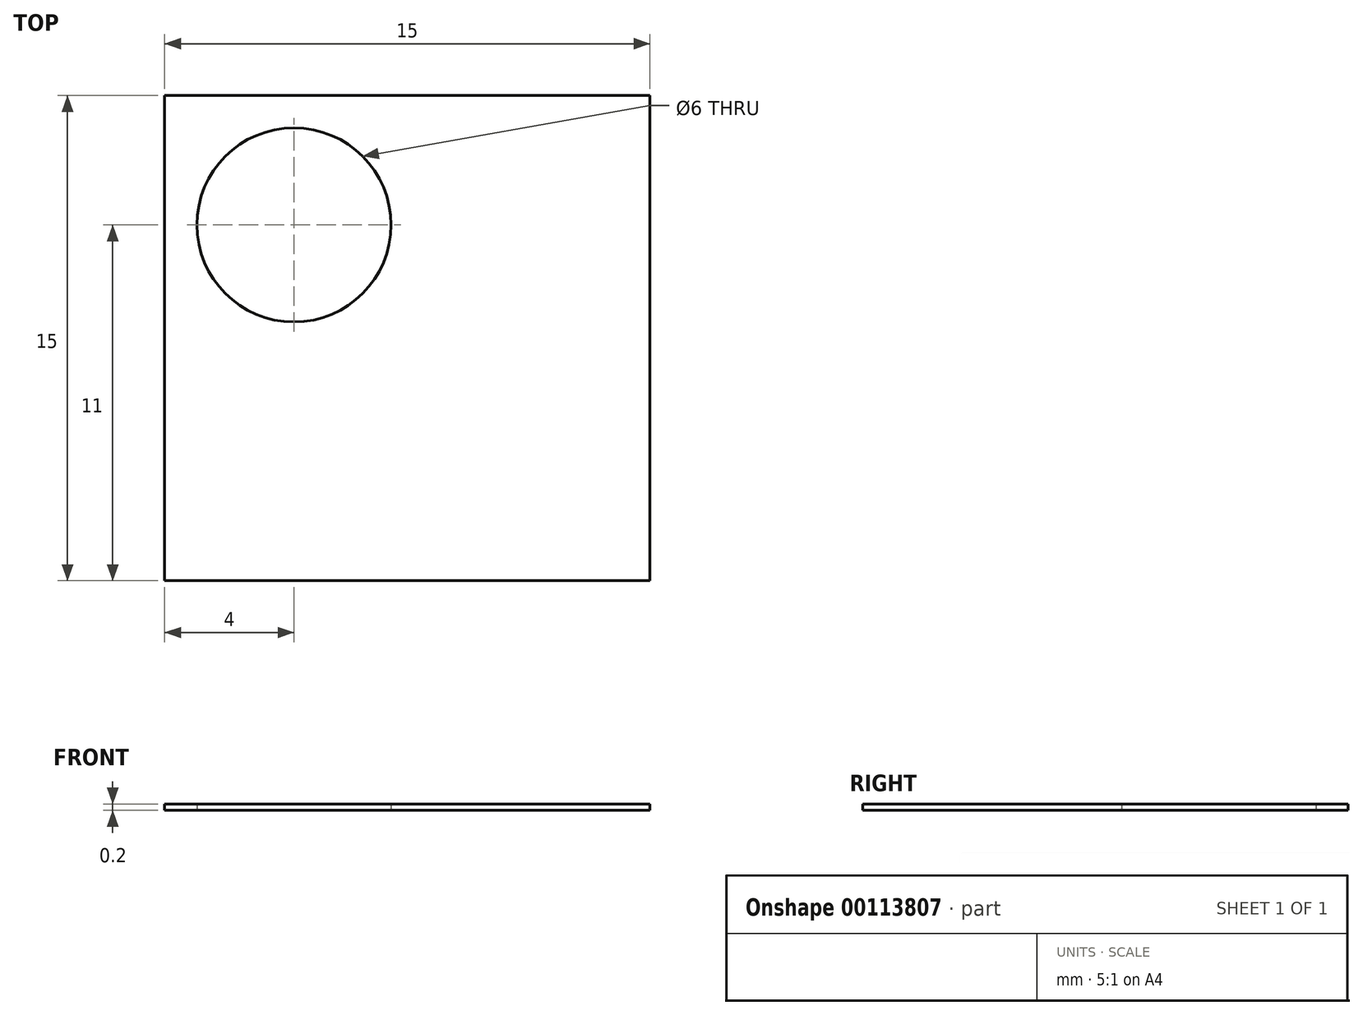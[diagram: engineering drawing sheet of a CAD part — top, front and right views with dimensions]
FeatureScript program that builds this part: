
annotation { "Feature Type Name" : "Feature", "Feature Type Description" : "" }
export const myFeature = defineFeature(function(context is Context, id is Id, definition is map)
    precondition{}
    {
        {
            var Q0;
            Q0=qCreatedBy(makeId("Top.planeOp"),FACE);
            var sketch = newSketch(context, id + "F0", { "sketchPlane" : qUnion([Q0])});
            skLineSegment(sketch, "E0.bottom", {"start": v(0, 15) * mm, "end": v(15, 15) * mm});
            skLineSegment(sketch, "E0.top", {"start": v(0, 0) * mm, "end": v(15, 0) * mm});
            skLineSegment(sketch, "E0.left", {"start": v(0, 15) * mm, "end": v(0, 0) * mm});
            skLineSegment(sketch, "E0.right", {"start": v(15, 15) * mm, "end": v(15, 0) * mm});
            skCircle(sketch, "E1", {"center": v(4, 11) * mm, "radius": 3 * mm});
            skSolve(sketch);
        }
        {
            var Q0;
            Q0=makeQuery(id+"F0.imprint","IMPRINT",FACE,{"disambiguationData":[TD([[makeQuery(id+"F0.imprint","IMPRINT",EDGE,{"derivedFrom":sQuery(id+"F0.wireOp",EDGE,"E0.bottom")}),-1.0]])]});
            extrude(context, id + "F1", {"entities" : qUnion([Q0]), "depth" : 0.2 * mm});
        }
    });
